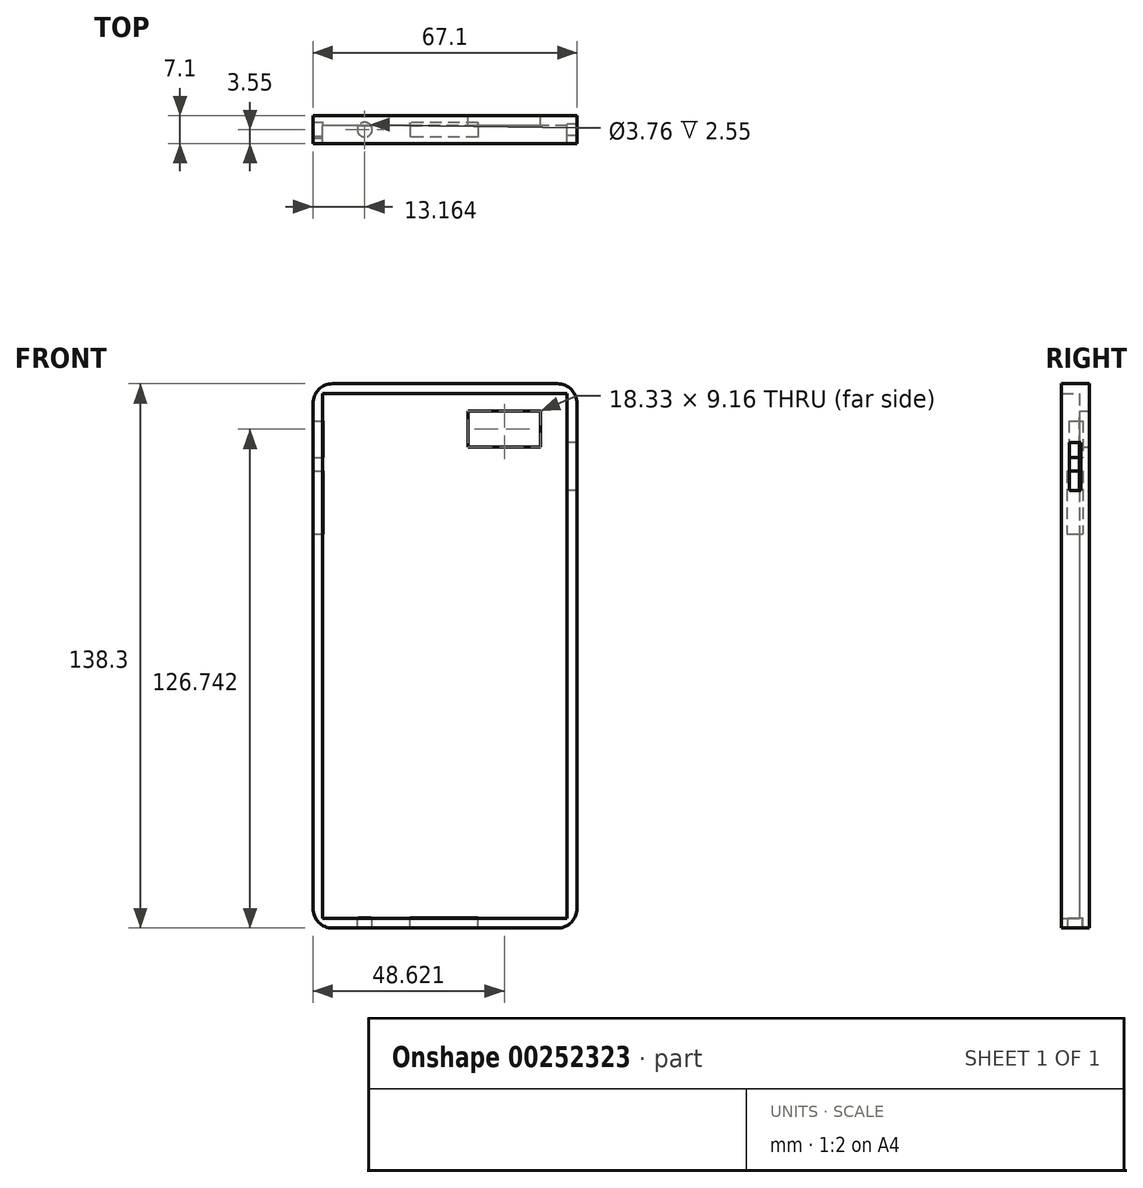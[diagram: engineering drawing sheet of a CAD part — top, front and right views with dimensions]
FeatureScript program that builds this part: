
annotation { "Feature Type Name" : "Feature", "Feature Type Description" : "" }
export const myFeature = defineFeature(function(context is Context, id is Id, definition is map)
    precondition{}
    {
        {
            var Q0;
            Q0=qCreatedBy(makeId("Front.planeOp"),FACE);
            var sketch = newSketch(context, id + "F0", { "sketchPlane" : qUnion([Q0])});
            skLineSegment(sketch, "E0.bottom", {"start": v(33.55, 69.15) * mm, "end": v(-33.55, 69.15) * mm});
            skLineSegment(sketch, "E0.top", {"start": v(33.55, -69.15) * mm, "end": v(-33.55, -69.15) * mm});
            skLineSegment(sketch, "E0.left", {"start": v(33.55, 69.15) * mm, "end": v(33.55, -69.15) * mm});
            skLineSegment(sketch, "E0.right", {"start": v(-33.55, 69.15) * mm, "end": v(-33.55, -69.15) * mm});
            skPoint(sketch, "E0.middle", {"position": v(0, 0) * mm});
            skSolve(sketch);
        }
        {
            var Q0;
            Q0=makeQuery(id+"F0.imprint","IMPRINT",FACE,{"disambiguationData":[TD([[makeQuery(id+"F0.imprint","IMPRINT",EDGE,{"derivedFrom":sQuery(id+"F0.wireOp",EDGE,"E0.bottom")}),1.0]])]});
            extrude(context, id + "F1", {"entities" : qUnion([Q0]), "endBound" : BoundingType.SYMMETRIC, "depth" : 7.1 * mm});
        }
        {
            var Q0;
            Q0=makeQuery(id+"F1.opExtrude","CAP_FACE",FACE,{"disambiguationData":[OSD([sQuery(id+"F0.wireOp",EDGE,"E0.bottom"),sQuery(id+"F0.wireOp",EDGE,"E0.top"),sQuery(id+"F0.wireOp",EDGE,"E0.left"),sQuery(id+"F0.wireOp",EDGE,"E0.right")])],"isStart":false});
            shell(context, id + "F2", {"entities" : qUnion([Q0]), "thickness" : 2.5 * mm});
        }
        {
            var Q0;
            Q0=makeQuery(id+"F1.opExtrude","SWEPT_EDGE",EDGE,{"disambiguationData":[OSD([sQuery(id+"F0.wireOp",EDGE,"E0.bottom"),sQuery(id+"F0.wireOp",EDGE,"E0.right")])]});
            var Q1;
            Q1=makeQuery(id+"F1.opExtrude","SWEPT_EDGE",EDGE,{"disambiguationData":[OSD([sQuery(id+"F0.wireOp",EDGE,"E0.bottom"),sQuery(id+"F0.wireOp",EDGE,"E0.left")])]});
            var Q2;
            Q2=makeQuery(id+"F1.opExtrude","SWEPT_EDGE",EDGE,{"disambiguationData":[OSD([sQuery(id+"F0.wireOp",EDGE,"E0.top"),sQuery(id+"F0.wireOp",EDGE,"E0.right")])]});
            var Q3;
            Q3=makeQuery(id+"F1.opExtrude","SWEPT_EDGE",EDGE,{"disambiguationData":[OSD([sQuery(id+"F0.wireOp",EDGE,"E0.top"),sQuery(id+"F0.wireOp",EDGE,"E0.left")])]});
            fillet(context, id + "F3", {"entities" : qUnion([Q0, Q1, Q2, Q3]), "radius" : 5 * mm, "tangentPropagation" : true, "allowEdgeOverflow" : false});
        }
        {
            var Q0;
            Q0=qCreatedBy(makeId("Front.planeOp"),FACE);
            var sketch = newSketch(context, id + "F4", { "sketchPlane" : qUnion([Q0])});
            skLineSegment(sketch, "E1.bottom", {"start": v(5.9, 62.17) * mm, "end": v(24.23, 62.17) * mm});
            skLineSegment(sketch, "E1.top", {"start": v(5.9, 53.01) * mm, "end": v(24.23, 53.01) * mm});
            skLineSegment(sketch, "E1.left", {"start": v(5.9, 62.17) * mm, "end": v(5.9, 53.01) * mm});
            skLineSegment(sketch, "E1.right", {"start": v(24.23, 62.17) * mm, "end": v(24.23, 53.01) * mm});
            skSolve(sketch);
        }
        {
            var Q0;
            Q0=makeQuery(id+"F4.imprint","IMPRINT",FACE,{"disambiguationData":[TD([[makeQuery(id+"F4.imprint","IMPRINT",EDGE,{"derivedFrom":sQuery(id+"F4.wireOp",EDGE,"E1.bottom")}),-1.0]])]});
            extrude(context, id + "F5", {"entities" : qUnion([Q0]), "operationType" : NewBodyOperationType.REMOVE, "endBound" : BoundingType.SYMMETRIC, "depth" : 25 * mm});
        }
        {
            var Q0;
            Q0=makeQuery(id+"F1.opExtrude","SWEPT_FACE",FACE,{"disambiguationData":[OSD([sQuery(id+"F0.wireOp",EDGE,"E0.top")])]});
            var sketch = newSketch(context, id + "F6", { "sketchPlane" : qUnion([Q0])});
            skLineSegment(sketch, "E2.bottom", {"start": v(-8.83, 1.88) * mm, "end": v(8.34, 1.88) * mm});
            skLineSegment(sketch, "E2.top", {"start": v(-8.83, -1.8) * mm, "end": v(8.34, -1.8) * mm});
            skLineSegment(sketch, "E2.left", {"start": v(-8.83, 1.88) * mm, "end": v(-8.83, -1.8) * mm});
            skLineSegment(sketch, "E2.right", {"start": v(8.34, 1.88) * mm, "end": v(8.34, -1.8) * mm});
            skSolve(sketch);
        }
        {
            var Q0;
            Q0 = qSketchRegion(id + "F6", true);
            extrude(context, id + "F7", {"entities" : qUnion([Q0]), "operationType" : NewBodyOperationType.REMOVE, "endBound" : BoundingType.SYMMETRIC, "depth" : 5.1 * mm});
        }
        {
            var Q0;
            Q0=makeQuery(id+"F1.opExtrude","SWEPT_FACE",FACE,{"disambiguationData":[OSD([sQuery(id+"F0.wireOp",EDGE,"E0.right")])]});
            var sketch = newSketch(context, id + "F8", { "sketchPlane" : qUnion([Q0])});
            skLineSegment(sketch, "E3.bottom", {"start": v(1.6, 59.7) * mm, "end": v(-1.87, 59.7) * mm});
            skLineSegment(sketch, "E3.top", {"start": v(1.6, 50.37) * mm, "end": v(-1.87, 50.37) * mm});
            skLineSegment(sketch, "E3.left", {"start": v(1.6, 59.7) * mm, "end": v(1.6, 50.37) * mm});
            skLineSegment(sketch, "E3.right", {"start": v(-1.87, 59.7) * mm, "end": v(-1.87, 50.37) * mm});
            skSolve(sketch);
        }
        {
            var Q0;
            Q0=makeQuery(id+"F8.imprint","IMPRINT",FACE,{"disambiguationData":[TD([[makeQuery(id+"F8.imprint","IMPRINT",EDGE,{"derivedFrom":sQuery(id+"F8.wireOp",EDGE,"E3.bottom")}),1.0]])]});
            extrude(context, id + "F9", {"entities" : qUnion([Q0]), "operationType" : NewBodyOperationType.REMOVE, "endBound" : BoundingType.SYMMETRIC, "depth" : 5.1 * mm});
        }
        {
            var Q0;
            Q0=makeQuery(id+"F1.opExtrude","SWEPT_FACE",FACE,{"disambiguationData":[OSD([sQuery(id+"F0.wireOp",EDGE,"E0.right")])]});
            var sketch = newSketch(context, id + "F10", { "sketchPlane" : qUnion([Q0])});
            skLineSegment(sketch, "E4.bottom", {"start": v(2.1, 46.95) * mm, "end": v(-1.87, 46.95) * mm});
            skLineSegment(sketch, "E4.top", {"start": v(2.1, 30.98) * mm, "end": v(-1.87, 30.98) * mm});
            skLineSegment(sketch, "E4.left", {"start": v(2.1, 46.95) * mm, "end": v(2.1, 30.98) * mm});
            skLineSegment(sketch, "E4.right", {"start": v(-1.87, 46.95) * mm, "end": v(-1.87, 30.98) * mm});
            skSolve(sketch);
        }
        {
            var Q0;
            Q0 = qSketchRegion(id + "F10", true);
            extrude(context, id + "F11", {"entities" : qUnion([Q0]), "operationType" : NewBodyOperationType.REMOVE, "endBound" : BoundingType.SYMMETRIC, "depth" : 5.1 * mm});
        }
        {
            var Q0;
            Q0=makeQuery(id+"F1.opExtrude","SWEPT_FACE",FACE,{"disambiguationData":[OSD([sQuery(id+"F0.wireOp",EDGE,"E0.top")])]});
            var sketch = newSketch(context, id + "F12", { "sketchPlane" : qUnion([Q0])});
            skCircle(sketch, "E5", {"center": v(-20.39, 0) * mm, "radius": 1.88 * mm});
            skSolve(sketch);
        }
        {
            var Q0;
            Q0 = qSketchRegion(id + "F12", true);
            extrude(context, id + "F13", {"entities" : qUnion([Q0]), "operationType" : NewBodyOperationType.REMOVE, "endBound" : BoundingType.SYMMETRIC, "depth" : 5.1 * mm});
        }
        {
            var Q0;
            Q0=makeQuery(id+"F1.opExtrude","CAP_FACE",FACE,{"disambiguationData":[OSD([sQuery(id+"F0.wireOp",EDGE,"E0.bottom"),sQuery(id+"F0.wireOp",EDGE,"E0.top"),sQuery(id+"F0.wireOp",EDGE,"E0.left"),sQuery(id+"F0.wireOp",EDGE,"E0.right")])],"isStart":true});
            var sketch = newSketch(context, id + "F14", { "sketchPlane" : qUnion([Q0])});
            skLineSegment(sketch, "E6", {"start": v(-18.07, 22.8) * mm, "end": v(-18.07, -43.18) * mm});
            skCircle(sketch, "E7", {"center": v(0, 0) * mm, "radius": 18.15 * mm});
            skSolve(sketch);
        }
        {
            var Q0;
            Q0=sQuery(id+"F14.wireOp",EDGE,"E7");
            extrude(context, id + "F15", {"bodyType" : ToolBodyType.SURFACE, "surfaceEntities" : qUnion([Q0]), "depth" : 2 * mm});
        }
        {
            var Q0;
            Q0=sQuery(id+"F14.wireOp",EDGE,"E6");
            extrude(context, id + "F16", {"bodyType" : ToolBodyType.SURFACE, "surfaceEntities" : qUnion([Q0]), "depth" : 2 * mm});
        }
        {
            var Q0;
            Q0=makeQuery(id+"F1.opExtrude","SWEPT_FACE",FACE,{"disambiguationData":[OSD([sQuery(id+"F0.wireOp",EDGE,"E0.left")])]});
            var sketch = newSketch(context, id + "F17", { "sketchPlane" : qUnion([Q0])});
            skLineSegment(sketch, "E8.bottom", {"start": v(-1.53, 54.22) * mm, "end": v(1.46, 54.22) * mm});
            skLineSegment(sketch, "E8.top", {"start": v(-1.53, 42.05) * mm, "end": v(1.46, 42.05) * mm});
            skLineSegment(sketch, "E8.left", {"start": v(-1.53, 54.22) * mm, "end": v(-1.53, 42.05) * mm});
            skLineSegment(sketch, "E8.right", {"start": v(1.46, 54.22) * mm, "end": v(1.46, 42.05) * mm});
            skSolve(sketch);
        }
        {
            var Q0;
            Q0=makeQuery(id+"F17.imprint","IMPRINT",FACE,{"disambiguationData":[TD([[makeQuery(id+"F17.imprint","IMPRINT",EDGE,{"derivedFrom":sQuery(id+"F17.wireOp",EDGE,"E8.bottom")}),-1.0]])]});
            extrude(context, id + "F18", {"entities" : qUnion([Q0]), "operationType" : NewBodyOperationType.REMOVE, "endBound" : BoundingType.SYMMETRIC, "depth" : 5 * mm});
        }
    });
